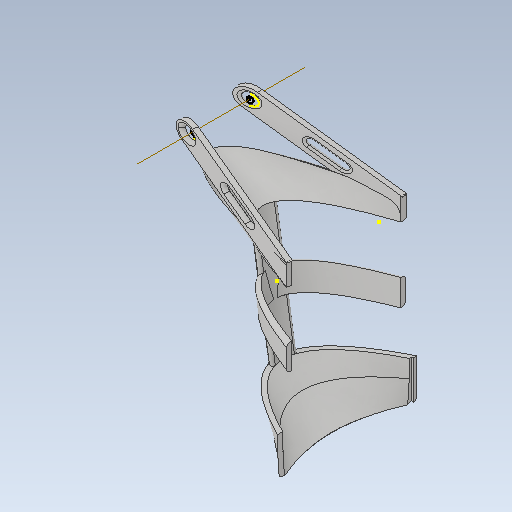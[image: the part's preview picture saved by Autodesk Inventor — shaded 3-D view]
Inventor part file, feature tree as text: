
AUTODESK INVENTOR PART (.ipt)
format: ipt  version: 2021 (Build 250183000, 183)  size: 1,364,992 bytes
history: native  units: in
note: dims shown in document units (in); Inventor stores cm internally (conversion verified against a paired STEP export)
features: sketch x37, fillet x17, plane x11, loft x5, other x5, extrude x2, mirror x1, direct_edit x1
ambient origin geometry x8: Origin, YZ Plane, XZ Plane, XY Plane, X Axis, Y Axis, Z Axis, Center Point
bodies: Solid1 (feature_tree)
feature tree (79):
  sketch  "Sketch1"  dims[d4=3.3858in d5=0.1575in]
  sketch  "Sketch2"  dims[d6=0.1575in d7=0.0in]
  sketch  "Sketch3"  dims[d8=2.7559in d9=0.1575in]
  sketch  "Sketch4"  dims[d10=0.9843in d11=4.4882in d12=0.9843in d13=0.0in d14=1.6929in d15=0.1575in d16=1.6929in d17=0.1575in d18=4.4882in d19=0.1575in]
  sketch  "Sketch5"  dims[d20=0.0in d21=90.0deg d22=0.0in d23=90.0deg d24=-5.5118in d25=1.9685in d26=0.1575in d27=1.9685in d28=0.1575in d29=1.9685in d30=0.1575in d31=-0.7874in]
  sketch  "Sketch6"  dims[d32=1.9685in d33=0.1575in d34=1.9685in d35=0.1575in d36=1.378in d37=0.1575in]
  plane  "Work Plane1"
  plane  "Work Plane3"
  sketch  "Sketch7"  dims[d38=0.0in d39=90.0deg d40=0.0in d41=90.0deg]
  sketch  "Sketch8"  dims[d44=0.3937in]
  loft  "Loft1"
  plane  "Work Plane4"
  sketch  "Sketch10"  dims[d46=0.3937in]
  sketch  "Sketch11"  dims[d47=90.0deg]
  plane  "Work Plane5"
  loft  "Loft2"
  sketch  "Sketch13"  dims[d49=0.1575in]
  sketch  "Sketch14"  dims[d53=0.3937in]
  sketch  "3D Sketch1"
  loft  "Loft3"
  plane  "Work Plane6"
  sketch  "Sketch17"  dims[d58=0.536in]
  sketch  "Sketch18"  dims[d59=1.9685in]
  extrude  "Extrusion1"  Depth=4.4882in
  mirror  "Mirror1"
  fillet  "Fillet1"  Radius=0.9843in
  fillet  "Fillet2"  Radius=1.6929in
  fillet  "Fillet3"  Radius=0.1575in
  fillet  "Fillet4"  Radius=1.6929in
  fillet  "Fillet5"  Radius=0.1575in
  fillet  "Fillet6"  Radius=4.4882in
  fillet  "Fillet7"  Radius=0.1575in
  sketch  "Sketch20"  dims[d64=4.2087in]
  plane  "Work Plane7"
  sketch  "Sketch21"  dims[d65=90.0deg]
  loft  "Loft4"
  fillet  "Fillet8"  Radius=0.1575in
  fillet  "Fillet9"  Radius=1.9685in
  fillet  "Fillet10"  Radius=0.1575in
  fillet  "Fillet11"  Radius=1.9685in
  fillet  "Fillet12"  Radius=0.1575in
  fillet  "Fillet13"  [1 undecoded]
  sketch  "Sketch23"  dims[d68=0.7581in]
  plane  "Work Plane8"
  sketch  "Sketch24"  dims[d69=0.9449in]
  sketch  "Sketch25"  dims[d70=0.2953in]
  plane  "Work Plane9"
  sketch  "Sketch26"  dims[d71=0.1575in d72=0.0in]
  sketch  "Sketch27"  dims[d73=0.0787in]
  sketch  "Sketch28"  dims[d74=0.0787in]
  sketch  "Sketch29"  dims[d75=0.0787in]
  sketch  "Sketch30"  dims[d76=0.0787in]
  sketch  "Sketch31"  dims[d77=0.0787in]
  sketch  "Sketch32"  dims[d78=0.0787in]
  plane  "Work Plane10"
  loft  "Loft5"
  fillet  "Fillet14"  Radius=1.9685in
  fillet  "Fillet15"  Radius=0.1575in
  fillet  "Fillet16"  Radius=1.378in
  fillet  "Fillet17"  Radius=0.1575in
  direct_edit  "Direct Edit1"
  plane  "Work Plane11"
  extrude  "Extrusion2"  TaperAngle=0.0deg  [1 undecoded]
  sketch  "Sketch35"  dims[d81=0.0787in]
  sketch  "Sketch36"  dims[d82=0.4724in d83=0.0in d84=90.0deg d85=0.0in d86=90.0deg d87=0.1575in d88=0.1181in d89=0.1181in d90=0.1181in d91=0.1181in d92=0.1181in d93=2.7559in d94=0.5906in d95=-1.1811in d96=0.0in d97=90.0deg d98=0.0in d99=90.0deg d100=0.1575in d101=0.1575in d102=0.1575in d103=0.1575in d104=0.3937in d105=0.2953in d106=0.3937in d107=0.3937in d108=0.3937in d109=0.4331in d110=0.4331in d111=0.3937in d112=0.3937in d113=0.25in d114=5.5118in d115=8.2677in d116=0.3937in d117=0.0in]
  other  "Work Axis1"
  plane  "Work Plane2"
  sketch  "Sketch9"  dims[d45=90.0deg]
  sketch  "Sketch12"  dims[d48=0.3937in]
  sketch  "Sketch15"  dims[d54=0.0in d55=90.0deg]
  sketch  "Sketch16"  dims[d56=0.0in d57=90.0deg]
  sketch  "Sketch19"  dims[d60=3.7834in]
  sketch  "Sketch22"  dims[d67=0.4724in]
  other  "Edges1"
  sketch  "Sketch33"  dims[d79=0.0787in]
  sketch  "Sketch34"  dims[d80=0.9843in]
  other  "Scale1"
  other  "Scale2"
  other  "Scale3"
note: 2 required parameter values undecoded (feature->parameter linkage not recoverable at this tier; creation-order binding heuristic only, values carry confidence <= 0.55)
